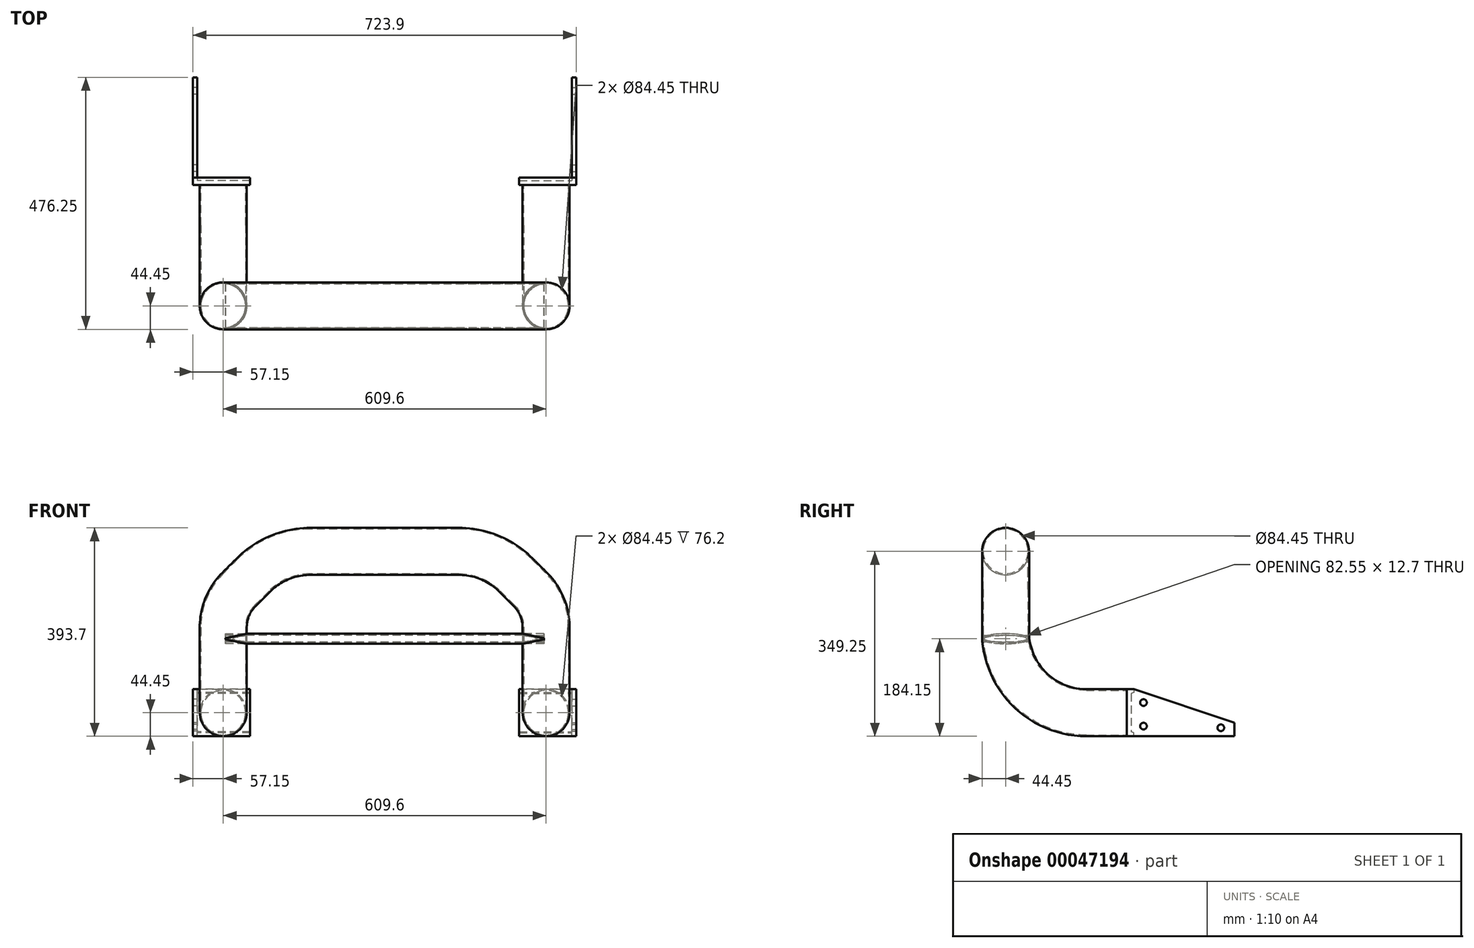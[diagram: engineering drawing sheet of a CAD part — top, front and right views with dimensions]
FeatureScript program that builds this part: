
annotation { "Feature Type Name" : "Feature", "Feature Type Description" : "" }
export const myFeature = defineFeature(function(context is Context, id is Id, definition is map)
    precondition{}
    {
        {
            var Q0;
            Q0=qCreatedBy(makeId("Right.planeOp"),FACE);
            cPlane(context, id + "F0", {"entities" : qUnion([Q0]), "cplaneType" : CPlaneType.OFFSET, "offset" : 304.8 * mm, "width" : 152.4 * mm, "height" : 152.4 * mm});
        }
        {
            var Q0;
            Q0=qCreatedBy(id+"F0.planeOp",FACE);
            var sketch = newSketch(context, id + "F1", { "sketchPlane" : qUnion([Q0])});
            skLineSegment(sketch, "E0", {"start": v(0, 0) * mm, "end": v(0, -6.35) * mm});
            skLineSegment(sketch, "E1", {"start": v(3.13, -31.36) * mm, "end": v(4.69, -37.51) * mm});
            skLineSegment(sketch, "E2", {"start": v(152.4, -152.4) * mm, "end": v(228.6, -152.4) * mm});
            skPoint(sketch, "E3.visualSharp", {"position": v(0, -19.05) * mm});
            skArc(sketch, "E3.filletArc", {"start": v(0, -6.35) * mm, "mid": v(0.78, -18.95) * mm, "end": v(3.13, -31.36) * mm});
            skPoint(sketch, "E4.visualSharp", {"position": v(33.87, -152.4) * mm});
            skArc(sketch, "E4.filletArc", {"start": v(4.69, -37.51) * mm, "mid": v(58.84, -120.3) * mm, "end": v(152.4, -152.4) * mm});
            skSolve(sketch);
        }
        {
            var Q0;
            Q0=qCreatedBy(makeId("Front.planeOp"),FACE);
            var sketch = newSketch(context, id + "F2", { "sketchPlane" : qUnion([Q0])});
            skLineSegment(sketch, "E5", {"start": v(304.8, 0) * mm, "end": v(304.8, 8.72) * mm});
            skLineSegment(sketch, "E6", {"start": v(275.04, 80.56) * mm, "end": v(247.84, 107.76) * mm});
            skLineSegment(sketch, "E7", {"start": v(140.07, 152.4) * mm, "end": v(0, 152.4) * mm});
            skPoint(sketch, "E8.visualSharp", {"position": v(203.2, 152.4) * mm});
            skArc(sketch, "E8.filletArc", {"start": v(247.84, 107.76) * mm, "mid": v(198.4, 140.8) * mm, "end": v(140.07, 152.4) * mm});
            skPoint(sketch, "E9.visualSharp", {"position": v(304.8, 50.8) * mm});
            skArc(sketch, "E9.filletArc", {"start": v(304.8, 8.72) * mm, "mid": v(297.07, 47.6) * mm, "end": v(275.04, 80.56) * mm});
            skSolve(sketch);
        }
        {
            var Q0;
            Q0=qCreatedBy(makeId("Top.planeOp"),FACE);
            var sketch = newSketch(context, id + "F3", { "sketchPlane" : qUnion([Q0])});
            skCircle(sketch, "E10", {"center": v(304.8, 0) * mm, "radius": 44.45 * mm});
            skCircle(sketch, "E11", {"center": v(304.8, 0) * mm, "radius": 42.23 * mm});
            skSolve(sketch);
        }
        {
            var Q0;
            Q0 = qSketchRegion(id + "F3", true);
            var Q1;
            Q1 = qConstructionFilter(qBodyType(qCreatedBy(id + "F1" ,EDGE), BodyType.WIRE), ConstructionObject.NO);
            sweep(context, id + "F4", {"profiles" : qUnion([Q0]), "path" : qUnion([Q1])});
        }
        {
            var Q0;
            Q0 = qSketchRegion(id + "F3", true);
            var Q1;
            Q1 = qConstructionFilter(qBodyType(qCreatedBy(id + "F2" ,EDGE), BodyType.WIRE), ConstructionObject.NO);
            sweep(context, id + "F5", {"operationType" : NewBodyOperationType.ADD, "profiles" : qUnion([Q0]), "path" : qUnion([Q1])});
        }
        {
            var Q0;
            Q0=qCreatedBy(makeId("Right.planeOp"),FACE);
            var sketch = newSketch(context, id + "F6", { "sketchPlane" : qUnion([Q0])});
            skEllipse(sketch, "E12", {"center": v(0, -12.7) * mm, "majorRadius": 44.45 * mm, "minorRadius": 9.53 * mm, "majorAxis": v(-1, 0)});
            skEllipse(sketch, "E13", {"center": v(0, -12.7) * mm, "majorRadius": 41.28 * mm, "minorRadius": 6.35 * mm, "majorAxis": v(-1, 0)});
            skSolve(sketch);
        }
        {
            var Q0;
            Q0 = qSketchRegion(id + "F6", true);
            var Q1;
            Q1=makeQuery(id+"F4.opSweep","SWEPT_FACE",FACE,{"disambiguationData":[OSD([sQuery(id+"F1.wireOp",EDGE,"E3.filletArc"),sQuery(id+"F3.wireOp",EDGE,"E10")])]});
            extrude(context, id + "F7", {"entities" : qUnion([Q0]), "operationType" : NewBodyOperationType.ADD, "endBoundEntityFace" : qUnion([Q1]), "depth" : 300.68 * mm});
        }
        {
            var Q0;
            Q0=makeQuery(id+"F4.opSweep","CAP_FACE",FACE,{"disambiguationData":[OSD([sQuery(id+"F1.wireOp",VERTEX,"E2.end"),sQuery(id+"F3.wireOp",EDGE,"E10"),sQuery(id+"F3.wireOp",EDGE,"E11")])],"isStart":false});
            var sketch = newSketch(context, id + "F8", { "sketchPlane" : qUnion([Q0])});
            skLineSegment(sketch, "E14.bottom", {"start": v(-361.95, -107.95) * mm, "end": v(-254, -107.95) * mm});
            skLineSegment(sketch, "E14.top", {"start": v(-361.95, -196.85) * mm, "end": v(-254, -196.85) * mm});
            skLineSegment(sketch, "E14.left", {"start": v(-361.95, -107.95) * mm, "end": v(-361.95, -196.85) * mm});
            skLineSegment(sketch, "E14.right", {"start": v(-254, -107.95) * mm, "end": v(-254, -196.85) * mm});
            skSolve(sketch);
        }
        {
            var Q0;
            Q0 = qSketchRegion(id + "F8", true);
            extrude(context, id + "F9", {"entities" : qUnion([Q0]), "operationType" : NewBodyOperationType.ADD, "depth" : 8.25 * mm});
        }
        {
            var Q0;
            Q0=makeQuery(id+"F9.opExtrude","SWEPT_FACE",FACE,{"disambiguationData":[OSD([sQuery(id+"F8.wireOp",EDGE,"E14.left")])]});
            var sketch = newSketch(context, id + "F10", { "sketchPlane" : qUnion([Q0])});
            skLineSegment(sketch, "E15", {"start": v(236.86, -107.95) * mm, "end": v(242.42, -107.95) * mm});
            skLineSegment(sketch, "E16", {"start": v(236.86, -116.2) * mm, "end": v(236.86, -107.95) * mm});
            skLineSegment(sketch, "E17", {"start": v(236.86, -116.2) * mm, "end": v(242.42, -114.3) * mm});
            skLineSegment(sketch, "E18", {"start": v(242.42, -114.3) * mm, "end": v(242.42, -107.95) * mm});
            skLineSegment(sketch, "E19", {"start": v(219.25, -152.4) * mm, "end": v(275.66, -152.4) * mm, "construction": true});
            skLineSegment(sketch, "E20.MirrorCS", {"start": v(236.86, -196.85) * mm, "end": v(242.42, -196.85) * mm});
            skLineSegment(sketch, "E21.MirrorCS", {"start": v(236.86, -188.6) * mm, "end": v(236.86, -196.85) * mm});
            skLineSegment(sketch, "E22.MirrorCS", {"start": v(236.86, -188.6) * mm, "end": v(242.42, -190.5) * mm});
            skLineSegment(sketch, "E23.MirrorCS", {"start": v(242.42, -190.5) * mm, "end": v(242.42, -196.85) * mm});
            skSolve(sketch);
        }
        {
            var Q0;
            Q0 = qSketchRegion(id + "F10", true);
            extrude(context, id + "F11", {"entities" : qUnion([Q0]), "operationType" : NewBodyOperationType.ADD, "oppositeDirection" : true, "depth" : 107.95 * mm});
        }
        {
            var Q0;
            Q0=makeQuery(id+"F11.boolean.opBoolean","MERGE",FACE,{"derivedFrom":[makeQuery(id+"F9.opExtrude","SWEPT_FACE",FACE,{"disambiguationData":[OSD([sQuery(id+"F8.wireOp",EDGE,"E14.left")])]}),makeQuery(id+"F11.opExtrude","CAP_FACE",FACE,{"disambiguationData":[OSD([sQuery(id+"F10.wireOp",EDGE,"E15"),sQuery(id+"F10.wireOp",EDGE,"E16"),sQuery(id+"F10.wireOp",EDGE,"E17"),sQuery(id+"F10.wireOp",EDGE,"E18")])],"isStart":true}),makeQuery(id+"F11.opExtrude","CAP_FACE",FACE,{"disambiguationData":[OSD([sQuery(id+"F10.wireOp",EDGE,"E20.MirrorCS"),sQuery(id+"F10.wireOp",EDGE,"E21.MirrorCS"),sQuery(id+"F10.wireOp",EDGE,"E22.MirrorCS"),sQuery(id+"F10.wireOp",EDGE,"E23.MirrorCS")])],"isStart":true})]});
            var sketch = newSketch(context, id + "F12", { "sketchPlane" : qUnion([Q0])});
            skLineSegment(sketch, "E24", {"start": v(228.6, -196.85) * mm, "end": v(431.8, -196.85) * mm});
            skLineSegment(sketch, "E25", {"start": v(431.8, -196.85) * mm, "end": v(431.8, -171.45) * mm});
            skLineSegment(sketch, "E26", {"start": v(431.8, -171.45) * mm, "end": v(242.42, -107.95) * mm});
            skLineSegment(sketch, "E27", {"start": v(242.42, -107.95) * mm, "end": v(228.6, -107.95) * mm});
            skLineSegment(sketch, "E28", {"start": v(228.6, -107.95) * mm, "end": v(228.6, -196.85) * mm});
            skCircle(sketch, "E29", {"center": v(260.35, -177.8) * mm, "radius": 6.35 * mm});
            skCircle(sketch, "E30", {"center": v(260.35, -133.35) * mm, "radius": 6.35 * mm});
            skCircle(sketch, "E31", {"center": v(406.4, -180.97) * mm, "radius": 6.35 * mm});
            skSolve(sketch);
        }
        {
            var Q0;
            Q0 = qSketchRegion(id + "F12", true);
            extrude(context, id + "F13", {"entities" : qUnion([Q0]), "operationType" : NewBodyOperationType.ADD, "oppositeDirection" : true, "depth" : 8.25 * mm});
        }
        {
            var Q0;
            Q0=makeQuery(id+"F4.opSweep","SWEPT_BODY",BODY,{"disambiguationData":[OSD([sQuery(id+"F1.wireOp",EDGE,"E2"),sQuery(id+"F3.wireOp",EDGE,"E10"),sQuery(id+"F3.wireOp",EDGE,"E11")])]});
            var Q1;
            Q1=qCreatedBy(makeId("Right.planeOp"),FACE);
            mirror(context, id + "F14", {"operationType" : NewBodyOperationType.ADD, "entities" : qUnion([Q0]), "mirrorPlane" : qUnion([Q1])});
        }
    });
